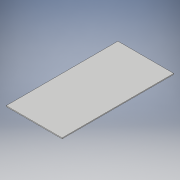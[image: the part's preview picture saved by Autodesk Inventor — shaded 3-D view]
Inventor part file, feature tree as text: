
AUTODESK INVENTOR PART (.ipt)
format: ipt  version: 2019 (Build 230136000, 136)  size: 95,232 bytes
history: native  units: mm
features: other x1, extrude x1, sketch x1
ambient origin geometry x8: Origin, YZ Plane, XZ Plane, XY Plane, X Axis, Y Axis, Z Axis, Center Point
bodies: Body1 (feature_tree)
feature tree (3):
  other  "ソリッド1"
  extrude  "押し出し1"  Depth=200.0mm
  sketch  "スケッチ1"
